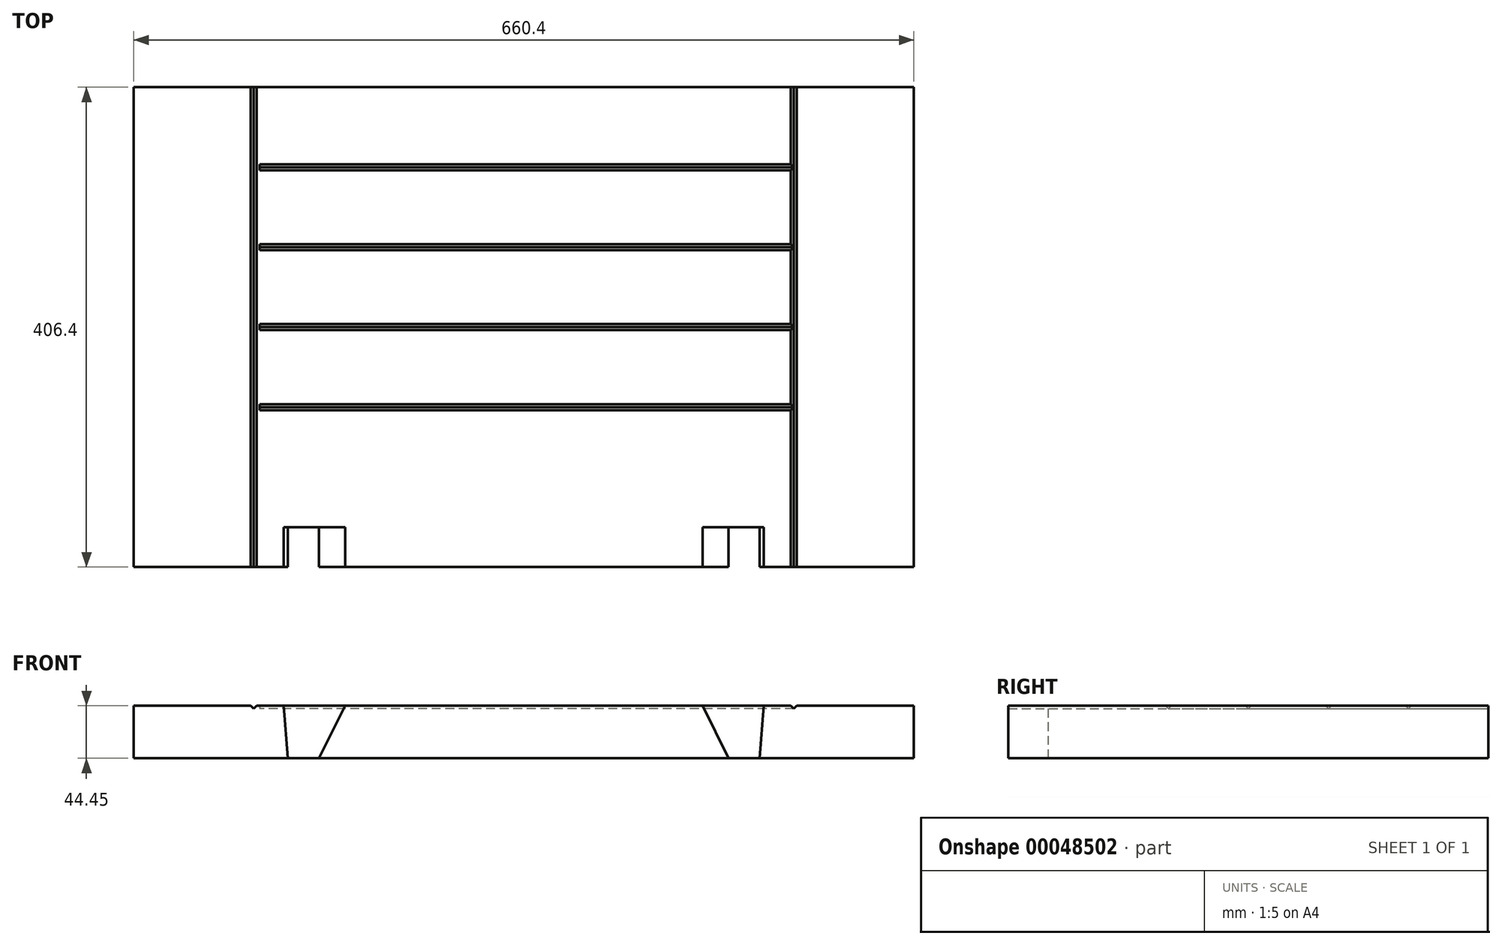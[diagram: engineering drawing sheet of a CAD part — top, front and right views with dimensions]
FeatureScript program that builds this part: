
annotation { "Feature Type Name" : "Feature", "Feature Type Description" : "" }
export const myFeature = defineFeature(function(context is Context, id is Id, definition is map)
    precondition{}
    {
        {
            var Q0;
            Q0=qCreatedBy(makeId("Top.planeOp"),FACE);
            var sketch = newSketch(context, id + "F0", { "sketchPlane" : qUnion([Q0])});
            skLineSegment(sketch, "E0.bottom", {"start": v(-330.2, 203.2) * mm, "end": v(330.2, 203.2) * mm});
            skLineSegment(sketch, "E0.top", {"start": v(-330.2, -203.2) * mm, "end": v(330.2, -203.2) * mm});
            skLineSegment(sketch, "E0.left", {"start": v(-330.2, 203.2) * mm, "end": v(-330.2, -203.2) * mm});
            skLineSegment(sketch, "E0.right", {"start": v(330.2, 203.2) * mm, "end": v(330.2, -203.2) * mm});
            skLineSegment(sketch, "E1", {"start": v(-228.6, 203.2) * mm, "end": v(-228.6, -203.2) * mm});
            skLineSegment(sketch, "E2", {"start": v(228.6, 203.2) * mm, "end": v(228.6, -203.2) * mm});
            skLineSegment(sketch, "E3", {"start": v(-228.6, 135.47) * mm, "end": v(228.6, 135.47) * mm});
            skLineSegment(sketch, "E4.0.1.0", {"start": v(-228.6, 67.73) * mm, "end": v(228.6, 67.73) * mm});
            skLineSegment(sketch, "E4.0.2.0", {"start": v(-228.6, 0) * mm, "end": v(228.6, 0) * mm});
            skLineSegment(sketch, "E4.0.3.0", {"start": v(-228.6, -67.73) * mm, "end": v(228.6, -67.73) * mm});
            skLineSegment(sketch, "E4.0.4.0", {"start": v(-228.6, -135.47) * mm, "end": v(228.6, -135.47) * mm});
            skLineSegment(sketch, "E4.0.5.0", {"start": v(-228.6, -203.2) * mm, "end": v(228.6, -203.2) * mm});
            skLineSegment(sketch, "E4.direction1", {"start": v(-228.6, 135.47) * mm, "end": v(-203.2, 135.47) * mm, "construction": true});
            skLineSegment(sketch, "E4.direction2", {"start": v(-228.6, 135.47) * mm, "end": v(-228.6, 67.73) * mm, "construction": true});
            skSolve(sketch);
        }
        {
            var Q0;
            {var subQ4=sQuery(id+"F0.wireOp",EDGE,"E0.left");Q0=makeQuery(id+"F0.imprint","IMPRINT",FACE,{"disambiguationData":[TD([[makeQuery(id+"F0.imprint","IMPRINT",EDGE,{"derivedFrom":subQ4}),1.0]])]});}
            var Q1;
            {var subQ3=sQuery(id+"F0.wireOp",EDGE,"E4.0.4.0");Q1=makeQuery(id+"F0.imprint","IMPRINT",FACE,{"disambiguationData":[TD([[makeQuery(id+"F0.imprint","IMPRINT",EDGE,{"derivedFrom":subQ3}),-1.0]])]});}
            var Q2;
            {var subQ0=sQuery(id+"F0.wireOp",EDGE,"E4.0.3.0");Q2=makeQuery(id+"F0.imprint","IMPRINT",FACE,{"disambiguationData":[TD([[makeQuery(id+"F0.imprint","IMPRINT",EDGE,{"derivedFrom":subQ0}),-1.0]])]});}
            var Q3;
            {var subQ0=sQuery(id+"F0.wireOp",EDGE,"E4.0.2.0");Q3=makeQuery(id+"F0.imprint","IMPRINT",FACE,{"disambiguationData":[TD([[makeQuery(id+"F0.imprint","IMPRINT",EDGE,{"derivedFrom":subQ0}),-1.0]])]});}
            var Q4;
            {var subQ0=sQuery(id+"F0.wireOp",EDGE,"E4.0.1.0");Q4=makeQuery(id+"F0.imprint","IMPRINT",FACE,{"disambiguationData":[TD([[makeQuery(id+"F0.imprint","IMPRINT",EDGE,{"derivedFrom":subQ0}),-1.0]])]});}
            var Q5;
            {var subQ0=sQuery(id+"F0.wireOp",EDGE,"E3");Q5=makeQuery(id+"F0.imprint","IMPRINT",FACE,{"disambiguationData":[TD([[makeQuery(id+"F0.imprint","IMPRINT",EDGE,{"derivedFrom":subQ0}),-1.0]])]});}
            var Q6;
            {var subQ5=sQuery(id+"F0.wireOp",EDGE,"E3");Q6=makeQuery(id+"F0.imprint","IMPRINT",FACE,{"disambiguationData":[TD([[makeQuery(id+"F0.imprint","IMPRINT",EDGE,{"derivedFrom":subQ5}),1.0]])]});}
            var Q7;
            {var subQ4=sQuery(id+"F0.wireOp",EDGE,"E0.right");Q7=makeQuery(id+"F0.imprint","IMPRINT",FACE,{"disambiguationData":[TD([[makeQuery(id+"F0.imprint","IMPRINT",EDGE,{"derivedFrom":subQ4}),-1.0]])]});}
            extrude(context, id + "F1", {"entities" : qUnion([Q0, Q1, Q2, Q3, Q4, Q5, Q6, Q7]), "depth" : 44.45 * mm});
        }
        {
            var Q0;
            Q0=makeQuery(id+"F1.opExtrude","CAP_FACE",FACE,{"disambiguationData":[OSD([sQuery(id+"F0.wireOp",EDGE,"E0.bottom"),sQuery(id+"F0.wireOp",EDGE,"E0.top"),sQuery(id+"F0.wireOp",EDGE,"E0.left"),sQuery(id+"F0.wireOp",EDGE,"E0.right"),sQuery(id+"F0.wireOp",EDGE,"E4.0.5.0")])],"isStart":false});
            var sketch = newSketch(context, id + "F2", { "sketchPlane" : qUnion([Q0])});
            skLineSegment(sketch, "E5", {"start": v(-228.6, 203.2) * mm, "end": v(-228.6, -203.2) * mm});
            skLineSegment(sketch, "E6", {"start": v(228.6, -203.2) * mm, "end": v(228.6, 203.2) * mm});
            skSolve(sketch);
        }
        {
            var Q0;
            Q0=makeQuery(id+"F1.opExtrude","SWEPT_FACE",FACE,{"disambiguationData":[OSD([sQuery(id+"F0.wireOp",EDGE,"E0.top"),sQuery(id+"F0.wireOp",EDGE,"E4.0.5.0")])]});
            var sketch = newSketch(context, id + "F3", { "sketchPlane" : qUnion([Q0])});
            skLineSegment(sketch, "E7.0.1", {"start": v(-228.6, 44.45) * mm, "end": v(-330.2, 44.45) * mm});
            skLineSegment(sketch, "E7.0.3", {"start": v(-330.2, 44.45) * mm, "end": v(-228.6, 44.45) * mm});
            skLineSegment(sketch, "E8.0.1", {"start": v(228.6, 44.45) * mm, "end": v(330.2, 44.45) * mm});
            skLineSegment(sketch, "E8.0.3", {"start": v(330.2, 44.45) * mm, "end": v(228.6, 44.45) * mm});
            skLineSegment(sketch, "E9", {"start": v(-228.6, 44.45) * mm, "end": v(-226.06, 44.45) * mm});
            skLineSegment(sketch, "E10", {"start": v(-226.06, 44.45) * mm, "end": v(-228.6, 41.91) * mm});
            skLineSegment(sketch, "E11", {"start": v(-228.6, 41.91) * mm, "end": v(-231.14, 44.45) * mm});
            skLineSegment(sketch, "E12", {"start": v(228.6, 44.45) * mm, "end": v(226.06, 44.45) * mm});
            skLineSegment(sketch, "E13", {"start": v(226.06, 44.45) * mm, "end": v(228.6, 41.91) * mm});
            skLineSegment(sketch, "E14", {"start": v(228.6, 41.91) * mm, "end": v(231.14, 44.45) * mm});
            skLineSegment(sketch, "E15", {"start": v(231.14, 44.45) * mm, "end": v(228.6, 44.45) * mm});
            skSolve(sketch);
        }
        {
            var Q0;
            {var subQ0=sQuery(id+"F3.wireOp",EDGE,"E9");Q0=makeQuery(id+"F3.imprint","IMPRINT",FACE,{"disambiguationData":[TD([[makeQuery(id+"F3.imprint","IMPRINT",EDGE,{"derivedFrom":subQ0}),-1.0]])]});}
            var Q1;
            Q1=makeQuery(id+"F3.imprint","IMPRINT",FACE,{"disambiguationData":[TD([[makeQuery(id+"F3.imprint","IMPRINT",EDGE,{"derivedFrom":sQuery(id+"F3.wireOp",EDGE,"E12")}),-1.0]])]});
            var Q2;
            Q2=sQuery(id+"F2.wireOp",EDGE,"E5");
            sweep(context, id + "F4", {"operationType" : NewBodyOperationType.REMOVE, "profiles" : qUnion([Q0, Q1]), "path" : qUnion([Q2])});
        }
        {
            var Q0;
            Q0=qCreatedBy(makeId("Right.planeOp"),FACE);
            cPlane(context, id + "F5", {"entities" : qUnion([Q0]), "cplaneType" : CPlaneType.OFFSET, "offset" : 228.6 * mm, "width" : 152.4 * mm, "height" : 152.4 * mm});
        }
        {
            var Q0;
            {var subQ0=sQuery(id+"F0.wireOp",EDGE,"E0.bottom");var subQ1=sQuery(id+"F2.wireOp",EDGE,"E5");var subQ2=sQuery(id+"F0.wireOp",EDGE,"E4.0.5.0");var subQ3=sQuery(id+"F0.wireOp",EDGE,"E0.top");Q0=makeQuery(id+"F4.boolean.opBoolean","SPLIT",FACE,{"disambiguationData":[TD([makeQuery(id+"F4.opSweep","SWEPT_FACE",FACE,{"disambiguationData":[OSD([subQ1,sQuery(id+"F3.wireOp",EDGE,"E10")])]})])],"derivedFrom":makeQuery(id+"F1.opExtrude","CAP_FACE",FACE,{"disambiguationData":[OSD([subQ0,subQ3,sQuery(id+"F0.wireOp",EDGE,"E0.left"),sQuery(id+"F0.wireOp",EDGE,"E0.right"),subQ2])],"isStart":false})});}
            var sketch = newSketch(context, id + "F6", { "sketchPlane" : qUnion([Q0])});
            skLineSegment(sketch, "E16.0", {"start": v(-226.06, 203.2) * mm, "end": v(226.06, 203.2) * mm});
            skLineSegment(sketch, "E17.0.1.0", {"start": v(-226.06, 135.47) * mm, "end": v(226.06, 135.47) * mm});
            skLineSegment(sketch, "E17.0.2.0", {"start": v(-226.06, 67.73) * mm, "end": v(226.06, 67.73) * mm});
            skLineSegment(sketch, "E17.0.3.0", {"start": v(-226.06, 0) * mm, "end": v(226.06, 0) * mm});
            skLineSegment(sketch, "E17.0.4.0", {"start": v(-226.06, -67.73) * mm, "end": v(226.06, -67.73) * mm});
            skLineSegment(sketch, "E17.0.5.0", {"start": v(-226.06, -135.47) * mm, "end": v(226.06, -135.47) * mm});
            skLineSegment(sketch, "E17.direction1", {"start": v(-226.06, 203.2) * mm, "end": v(-200.66, 203.2) * mm, "construction": true});
            skLineSegment(sketch, "E17.direction2", {"start": v(-226.06, 203.2) * mm, "end": v(-226.06, 135.47) * mm, "construction": true});
            skSolve(sketch);
        }
        {
            var Q0;
            Q0=qCreatedBy(id+"F5.planeOp",FACE);
            var sketch = newSketch(context, id + "F7", { "sketchPlane" : qUnion([Q0])});
            skLineSegment(sketch, "E18.0.1", {"start": v(-135.47, 44.45) * mm, "end": v(-203.2, 44.45) * mm});
            skLineSegment(sketch, "E18.0.3", {"start": v(-203.2, 44.45) * mm, "end": v(-135.47, 44.45) * mm});
            skLineSegment(sketch, "E19.0.1", {"start": v(-67.73, 44.45) * mm, "end": v(-135.47, 44.45) * mm});
            skLineSegment(sketch, "E19.0.3", {"start": v(-135.47, 44.45) * mm, "end": v(-67.73, 44.45) * mm});
            skLineSegment(sketch, "E20.0.1", {"start": v(0, 44.45) * mm, "end": v(-67.73, 44.45) * mm});
            skLineSegment(sketch, "E20.0.3", {"start": v(-67.73, 44.45) * mm, "end": v(0, 44.45) * mm});
            skLineSegment(sketch, "E21.0.1", {"start": v(67.73, 44.45) * mm, "end": v(0, 44.45) * mm});
            skLineSegment(sketch, "E21.0.3", {"start": v(0, 44.45) * mm, "end": v(67.73, 44.45) * mm});
            skLineSegment(sketch, "E22.0.1", {"start": v(135.47, 44.45) * mm, "end": v(67.73, 44.45) * mm});
            skLineSegment(sketch, "E22.0.3", {"start": v(67.73, 44.45) * mm, "end": v(135.47, 44.45) * mm});
            skLineSegment(sketch, "E23.0.0", {"start": v(203.2, 44.45) * mm, "end": v(135.47, 44.45) * mm});
            skLineSegment(sketch, "E23.0.2", {"start": v(135.47, 44.45) * mm, "end": v(203.2, 44.45) * mm});
            skLineSegment(sketch, "E24", {"start": v(-135.47, 44.45) * mm, "end": v(-132.93, 44.45) * mm});
            skLineSegment(sketch, "E25", {"start": v(-132.93, 44.45) * mm, "end": v(-135.47, 41.91) * mm});
            skLineSegment(sketch, "E26", {"start": v(-135.47, 41.91) * mm, "end": v(-138, 44.45) * mm});
            skLineSegment(sketch, "E27", {"start": v(-138, 44.45) * mm, "end": v(-135.47, 44.45) * mm});
            skLineSegment(sketch, "E28.1.0.0", {"start": v(-67.73, 41.91) * mm, "end": v(-70.27, 44.45) * mm});
            skLineSegment(sketch, "E28.1.0.1", {"start": v(-65.2, 44.45) * mm, "end": v(-67.73, 41.91) * mm});
            skLineSegment(sketch, "E28.2.0.0", {"start": v(0, 41.91) * mm, "end": v(-2.54, 44.45) * mm});
            skLineSegment(sketch, "E28.2.0.1", {"start": v(2.54, 44.45) * mm, "end": v(0, 41.91) * mm});
            skLineSegment(sketch, "E28.3.0.0", {"start": v(67.73, 41.91) * mm, "end": v(65.2, 44.45) * mm});
            skLineSegment(sketch, "E28.3.0.1", {"start": v(70.27, 44.45) * mm, "end": v(67.73, 41.91) * mm});
            skLineSegment(sketch, "E28.4.0.0", {"start": v(135.47, 41.91) * mm, "end": v(132.93, 44.45) * mm});
            skLineSegment(sketch, "E28.4.0.1", {"start": v(138, 44.45) * mm, "end": v(135.47, 41.91) * mm});
            skLineSegment(sketch, "E28.direction1", {"start": v(-135.47, 41.91) * mm, "end": v(-67.73, 41.91) * mm, "construction": true});
            skSolve(sketch);
        }
        {
            var Q0;
            Q0=makeQuery(id+"F7.imprint","IMPRINT",FACE,{"disambiguationData":[TD([[makeQuery(id+"F7.imprint","IMPRINT",EDGE,{"derivedFrom":sQuery(id+"F7.wireOp",EDGE,"E24")}),-1.0]])]});
            var Q1;
            {var subQ3=sQuery(id+"F7.wireOp",EDGE,"E28.1.0.0");Q1=makeQuery(id+"F7.imprint","IMPRINT",FACE,{"disambiguationData":[TD([[makeQuery(id+"F7.imprint","IMPRINT",EDGE,{"derivedFrom":subQ3}),-1.0]])]});}
            var Q2;
            {var subQ3=sQuery(id+"F7.wireOp",EDGE,"E28.2.0.0");Q2=makeQuery(id+"F7.imprint","IMPRINT",FACE,{"disambiguationData":[TD([[makeQuery(id+"F7.imprint","IMPRINT",EDGE,{"derivedFrom":subQ3}),-1.0]])]});}
            var Q3;
            {var subQ3=sQuery(id+"F7.wireOp",EDGE,"E28.3.0.0");Q3=makeQuery(id+"F7.imprint","IMPRINT",FACE,{"disambiguationData":[TD([[makeQuery(id+"F7.imprint","IMPRINT",EDGE,{"derivedFrom":subQ3}),-1.0]])]});}
            var Q4;
            {var subQ3=sQuery(id+"F7.wireOp",EDGE,"E28.4.0.0");Q4=makeQuery(id+"F7.imprint","IMPRINT",FACE,{"disambiguationData":[TD([[makeQuery(id+"F7.imprint","IMPRINT",EDGE,{"derivedFrom":subQ3}),-1.0]])]});}
            var Q5;
            Q5=sQuery(id+"F6.wireOp",EDGE,"E17.0.4.0");
            sweep(context, id + "F8", {"operationType" : NewBodyOperationType.REMOVE, "profiles" : qUnion([Q0, Q1, Q2, Q3, Q4]), "path" : qUnion([Q5])});
        }
        {
            var Q0;
            Q0=makeQuery(id+"F1.opExtrude","SWEPT_FACE",FACE,{"disambiguationData":[OSD([sQuery(id+"F0.wireOp",EDGE,"E0.top"),sQuery(id+"F0.wireOp",EDGE,"E4.0.5.0")])]});
            var sketch = newSketch(context, id + "F9", { "sketchPlane" : qUnion([Q0])});
            skPoint(sketch, "E29", {"position": v(203.2, 44.45) * mm});
            skLineSegment(sketch, "E30", {"start": v(203.2, 44.45) * mm, "end": v(203.2, -565.15) * mm, "construction": true});
            skLineSegment(sketch, "E31", {"start": v(203.2, -565.15) * mm, "end": v(330.2, -565.15) * mm, "construction": true});
            skLineSegment(sketch, "E32", {"start": v(330.2, -565.15) * mm, "end": v(203.2, 44.45) * mm, "construction": true});
            skLineSegment(sketch, "E33", {"start": v(151.3, 44.45) * mm, "end": v(171.59, -52.9) * mm});
            skLineSegment(sketch, "E34", {"start": v(171.59, -52.9) * mm, "end": v(278.3, -565.15) * mm});
            skLineSegment(sketch, "E35", {"start": v(199.76, 0) * mm, "end": v(212.46, 0) * mm});
            skLineSegment(sketch, "E36", {"start": v(160.57, 0) * mm, "end": v(173.27, 0) * mm});
            skLineSegment(sketch, "E37", {"start": v(199.76, 0) * mm, "end": v(203.2, 44.45) * mm});
            skLineSegment(sketch, "E38", {"start": v(173.27, 0) * mm, "end": v(151.3, 44.45) * mm});
            skLineSegment(sketch, "E39", {"start": v(151.3, 44.45) * mm, "end": v(203.2, 44.45) * mm});
            skLineSegment(sketch, "E40", {"start": v(173.27, 0) * mm, "end": v(199.76, 0) * mm});
            skLineSegment(sketch, "E41", {"start": v(0, 0) * mm, "end": v(0, 44.45) * mm, "construction": true});
            skLineSegment(sketch, "E42.MirrorCS", {"start": v(-173.27, 0) * mm, "end": v(-151.3, 44.45) * mm});
            skLineSegment(sketch, "E43.MirrorCS", {"start": v(-151.3, 44.45) * mm, "end": v(-203.2, 44.45) * mm});
            skLineSegment(sketch, "E44.MirrorCS", {"start": v(-199.76, 0) * mm, "end": v(-203.2, 44.45) * mm});
            skLineSegment(sketch, "E45.MirrorCS", {"start": v(-173.27, 0) * mm, "end": v(-199.76, 0) * mm});
            skSolve(sketch);
        }
        {
            var Q0;
            Q0=makeQuery(id+"F9.imprint","IMPRINT",FACE,{"disambiguationData":[TD([[makeQuery(id+"F9.imprint","IMPRINT",EDGE,{"derivedFrom":sQuery(id+"F9.wireOp",EDGE,"E42.MirrorCS")}),1.0]])]});
            var Q1;
            Q1=makeQuery(id+"F9.imprint","IMPRINT",FACE,{"disambiguationData":[TD([[makeQuery(id+"F9.imprint","IMPRINT",EDGE,{"derivedFrom":sQuery(id+"F9.wireOp",EDGE,"E37")}),1.0]])]});
            extrude(context, id + "F10", {"entities" : qUnion([Q0, Q1]), "operationType" : NewBodyOperationType.REMOVE, "oppositeDirection" : true, "depth" : 33.78 * mm});
        }
    });
